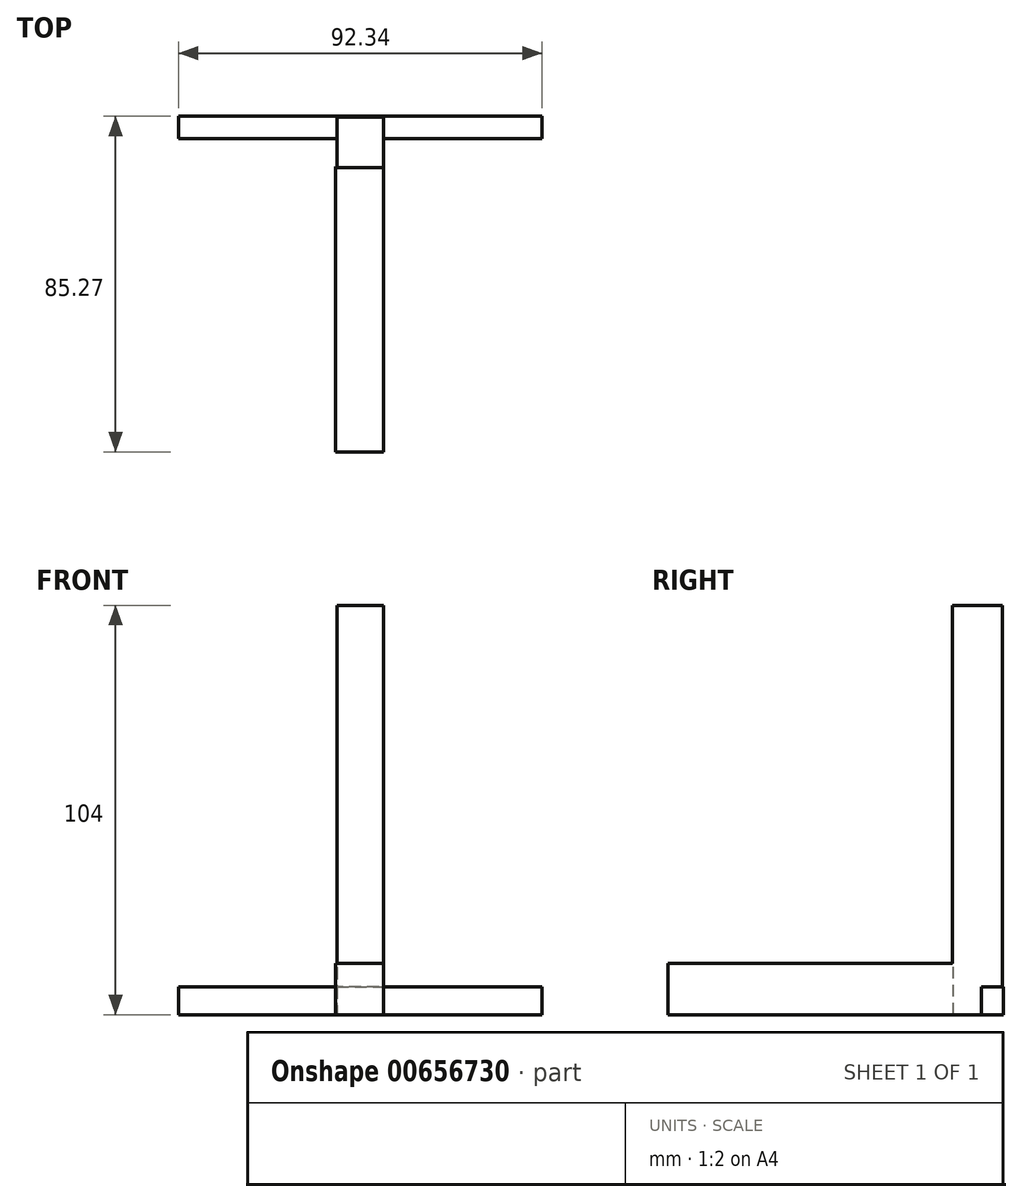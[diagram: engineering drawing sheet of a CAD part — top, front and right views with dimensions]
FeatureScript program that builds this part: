
annotation { "Feature Type Name" : "Feature", "Feature Type Description" : "" }
export const myFeature = defineFeature(function(context is Context, id is Id, definition is map)
    precondition{}
    {
        {
            var Q0;
            Q0=qCreatedBy(makeId("Top.planeOp"),FACE);
            var sketch = newSketch(context, id + "F0", { "sketchPlane" : qUnion([Q0])});
            skLineSegment(sketch, "E0.bottom", {"start": v(-16.29, 16.85) * mm, "end": v(-4.4, 16.85) * mm});
            skLineSegment(sketch, "E0.top", {"start": v(-16.29, 4.1) * mm, "end": v(-4.4, 4.1) * mm});
            skLineSegment(sketch, "E0.left", {"start": v(-16.29, 16.85) * mm, "end": v(-16.29, 4.1) * mm});
            skLineSegment(sketch, "E0.right", {"start": v(-4.4, 16.85) * mm, "end": v(-4.4, 4.1) * mm});
            skSolve(sketch);
        }
        {
            var Q0;
            Q0 = qSketchRegion(id + "F0", true);
            extrude(context, id + "F1", {"entities" : qUnion([Q0]), "depth" : 104 * mm, "offsetDistance" : 25 * mm});
        }
        {
            var Q0;
            Q0=qCreatedBy(makeId("Top.planeOp"),FACE);
            var sketch = newSketch(context, id + "F2", { "sketchPlane" : qUnion([Q0])});
            skLineSegment(sketch, "E1.bottom", {"start": v(-16.57, 4.4) * mm, "end": v(-4.4, 4.4) * mm});
            skLineSegment(sketch, "E1.top", {"start": v(-16.57, -68.13) * mm, "end": v(-4.4, -68.13) * mm});
            skLineSegment(sketch, "E1.left", {"start": v(-16.57, 4.4) * mm, "end": v(-16.57, -68.13) * mm});
            skLineSegment(sketch, "E1.right", {"start": v(-4.4, 4.4) * mm, "end": v(-4.4, -68.13) * mm});
            skSolve(sketch);
        }
        {
            var Q0;
            Q0 = qSketchRegion(id + "F2", true);
            extrude(context, id + "F3", {"entities" : qUnion([Q0]), "operationType" : NewBodyOperationType.ADD, "depth" : 13 * mm, "offsetDistance" : 25 * mm});
        }
        {
            var Q0;
            Q0=qCreatedBy(makeId("Top.planeOp"),FACE);
            var sketch = newSketch(context, id + "F4", { "sketchPlane" : qUnion([Q0])});
            skLineSegment(sketch, "E2.bottom", {"start": v(-4.17, 17.14) * mm, "end": v(35.83, 17.14) * mm});
            skLineSegment(sketch, "E2.top", {"start": v(-4.17, 11.47) * mm, "end": v(35.83, 11.47) * mm});
            skLineSegment(sketch, "E2.left", {"start": v(-4.17, 17.14) * mm, "end": v(-4.17, 11.47) * mm});
            skLineSegment(sketch, "E2.right", {"start": v(35.83, 17.14) * mm, "end": v(35.83, 11.47) * mm});
            skLineSegment(sketch, "E3.bottom", {"start": v(-16.51, 17.14) * mm, "end": v(-56.51, 17.14) * mm});
            skLineSegment(sketch, "E3.top", {"start": v(-16.51, 11.47) * mm, "end": v(-56.51, 11.47) * mm});
            skLineSegment(sketch, "E3.left", {"start": v(-16.51, 17.14) * mm, "end": v(-16.51, 11.47) * mm});
            skLineSegment(sketch, "E3.right", {"start": v(-56.51, 17.14) * mm, "end": v(-56.51, 11.47) * mm});
            skSolve(sketch);
        }
        {
            var Q0;
            Q0 = qSketchRegion(id + "F4", true);
            extrude(context, id + "F5", {"entities" : qUnion([Q0]), "depth" : 7 * mm, "offsetDistance" : 25 * mm});
        }
        {
            var Q0;
            Q0=makeQuery(id+"F5.opExtrude","SWEPT_FACE",FACE,{"disambiguationData":[OSD([sQuery(id+"F4.wireOp",EDGE,"E3.left")])]});
            extrude(context, id + "F6", {"entities" : qUnion([Q0]), "operationType" : NewBodyOperationType.ADD, "depth" : 12.1 * mm, "offsetDistance" : 25 * mm});
        }
        {
            var Q0;
            Q0=makeQuery(id+"F5.opExtrude","SWEPT_FACE",FACE,{"disambiguationData":[OSD([sQuery(id+"F4.wireOp",EDGE,"E2.left")])]});
            extrude(context, id + "F7", {"entities" : qUnion([Q0]), "operationType" : NewBodyOperationType.ADD, "depth" : 3 * mm, "offsetDistance" : 25 * mm});
        }
    });
